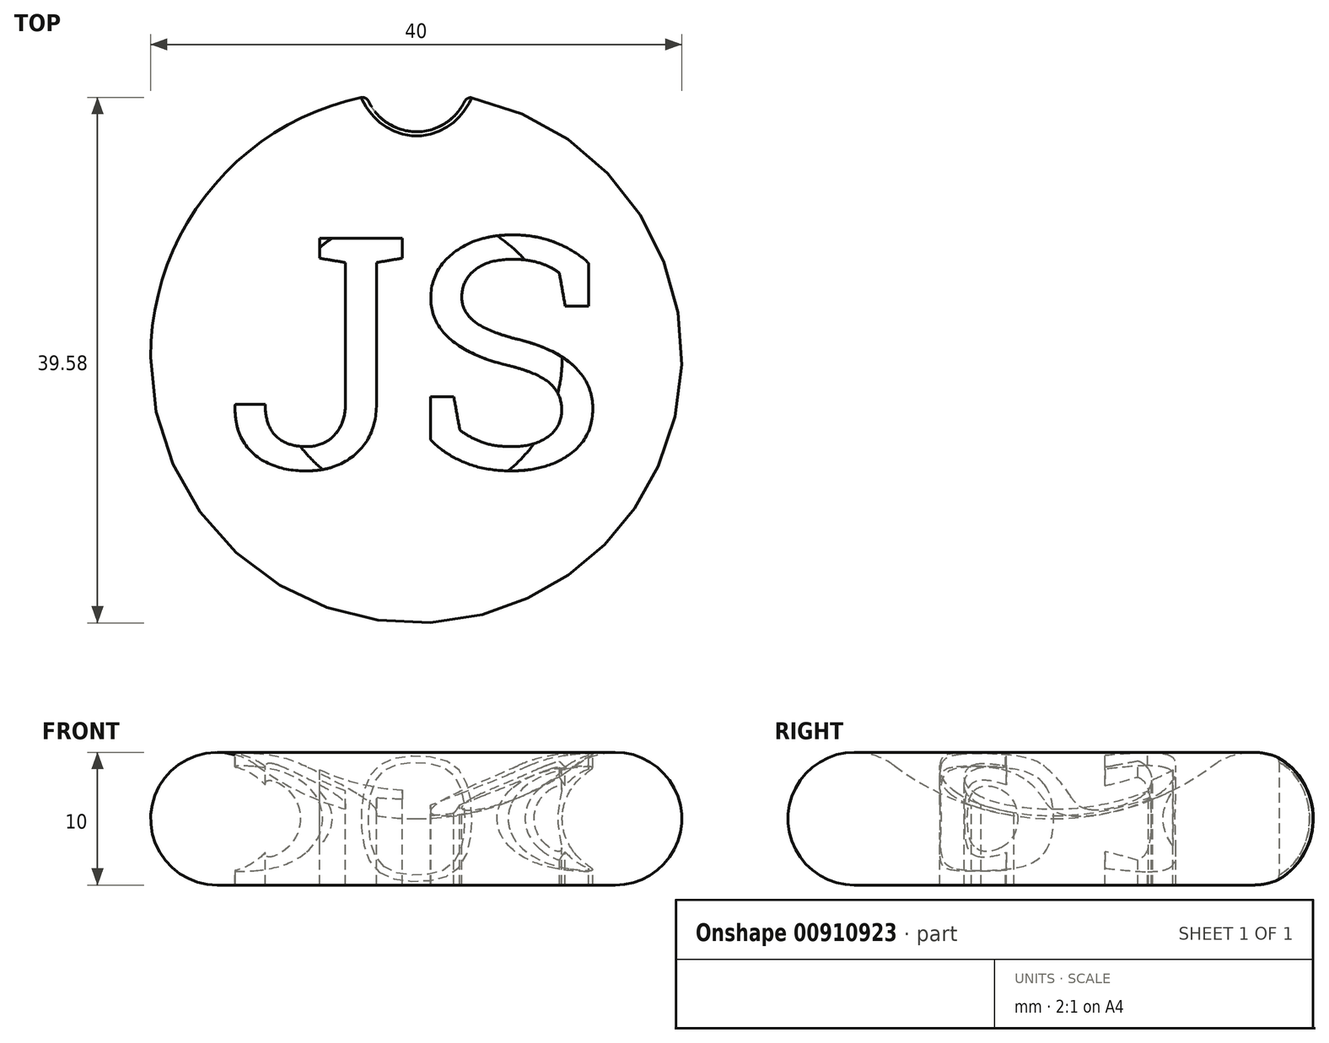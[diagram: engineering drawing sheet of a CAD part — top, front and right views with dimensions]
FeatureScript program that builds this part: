
annotation { "Feature Type Name" : "Feature", "Feature Type Description" : "" }
export const myFeature = defineFeature(function(context is Context, id is Id, definition is map)
    precondition{}
    {
        {
            var Q0;
            Q0=qCreatedBy(makeId("Front.planeOp"),FACE);
            var sketch = newSketch(context, id + "F0", { "sketchPlane" : qUnion([Q0])});
            skArc(sketch, "E0", {"start": v(-12, 9) * mm, "mid": v(-19.74, 6.58) * mm, "end": v(-15, 0) * mm});
            skArc(sketch, "E1", {"start": v(-12, 9) * mm, "mid": v(-6.32, 6.03) * mm, "end": v(0, 5) * mm});
            skLineSegment(sketch, "E2", {"start": v(-15, 0) * mm, "end": v(0, 0) * mm});
            skLineSegment(sketch, "E3", {"start": v(0, 0) * mm, "end": v(0, 5) * mm});
            skSolve(sketch);
        }
        {
            var Q0;
            Q0=makeQuery(id+"F0.imprint","IMPRINT",FACE,{"disambiguationData":[TD([[makeQuery(id+"F0.imprint","IMPRINT",EDGE,{"derivedFrom":sQuery(id+"F0.wireOp",EDGE,"E0")}),1.0]])]});
            var Q1;
            Q1=sQuery(id+"F0.wireOp",EDGE,"E3");
            revolve(context, id + "F1", {"surfaceOperationType" : NewSurfaceOperationType.NEW, "entities" : qUnion([Q0]), "axis" : qUnion([Q1]), "revolveType" : RevolveType.FULL});
        }
        {
            var Q0;
            Q0=qCreatedBy(makeId("Top.planeOp"),FACE);
            cPlane(context, id + "F2", {"entities" : qUnion([Q0]), "cplaneType" : CPlaneType.OFFSET, "offset" : 10 * mm, "width" : 150 * mm, "height" : 150 * mm});
        }
        {
            var Q0;
            Q0=qCreatedBy(id+"F2.planeOp",FACE);
            var sketch = newSketch(context, id + "F3", { "sketchPlane" : qUnion([Q0])});
            skText(sketch, "E4", { "text": "JS", "fontName": "RobotoSlab-Regular.ttf"});
            const initialGuessF3  = {"E4": [-0.0144, -0.0083, 1, 0, 0.0175]};
            skSetInitialGuess(sketch, initialGuessF3);
            skSolve(sketch);
        }
        {
            var Q0;
            Q0 = qSketchRegion(id + "F3", true);
            extrude(context, id + "F4", {"entities" : qUnion([Q0]), "operationType" : NewBodyOperationType.REMOVE, "endBound" : BoundingType.SYMMETRIC, "oppositeDirection" : true, "depth" : 25 * mm, "offsetDistance" : 25 * mm});
        }
        {
            var Q0;
            Q0=qCreatedBy(makeId("Front.planeOp"),FACE);
            var sketch = newSketch(context, id + "F5", { "sketchPlane" : qUnion([Q0])});
            skCircle(sketch, "E5", {"center": v(-15, 5) * mm, "radius": 4 * mm});
            skSolve(sketch);
        }
        {
            var Q0;
            Q0 = qSketchRegion(id + "F5", true);
            var Q1;
            Q1=sQuery(id+"F0.wireOp",EDGE,"E3");
            revolve(context, id + "F6", {"operationType" : NewBodyOperationType.ADD, "surfaceOperationType" : NewSurfaceOperationType.NEW, "entities" : qUnion([Q0]), "axis" : qUnion([Q1]), "revolveType" : RevolveType.FULL});
        }
        {
            var Q0;
            Q0=qCreatedBy(makeId("Top.planeOp"),FACE);
            var sketch = newSketch(context, id + "F7", { "sketchPlane" : qUnion([Q0])});
            skCircle(sketch, "E6", {"center": v(0.03, 21) * mm, "radius": 4 * mm});
            skSolve(sketch);
        }
        {
            var Q0;
            Q0=makeQuery(id+"F7.imprint","IMPRINT",FACE,{"disambiguationData":[TD([[makeQuery(id+"F7.imprint","IMPRINT",EDGE,{"derivedFrom":sQuery(id+"F7.wireOp",EDGE,"E6")}),1.0]])]});
            extrude(context, id + "F8", {"entities" : qUnion([Q0]), "operationType" : NewBodyOperationType.REMOVE, "endBound" : BoundingType.THROUGH_ALL, "depth" : 12.1 * mm, "offsetDistance" : 25 * mm});
        }
        {
            var Q0;
            Q0=makeQuery(id+"F8.boolean.opBoolean","COPY",FACE,{"derivedFrom":makeQuery(id+"F8.opExtrude","SWEPT_FACE",FACE,{"disambiguationData":[OSD([sQuery(id+"F7.wireOp",EDGE,"E6")])]})});
            fillet(context, id + "F9", {"entities" : qUnion([Q0]), "radius" : 0.5 * mm, "tangentPropagation" : true, "allowEdgeOverflow" : false});
        }
    });
